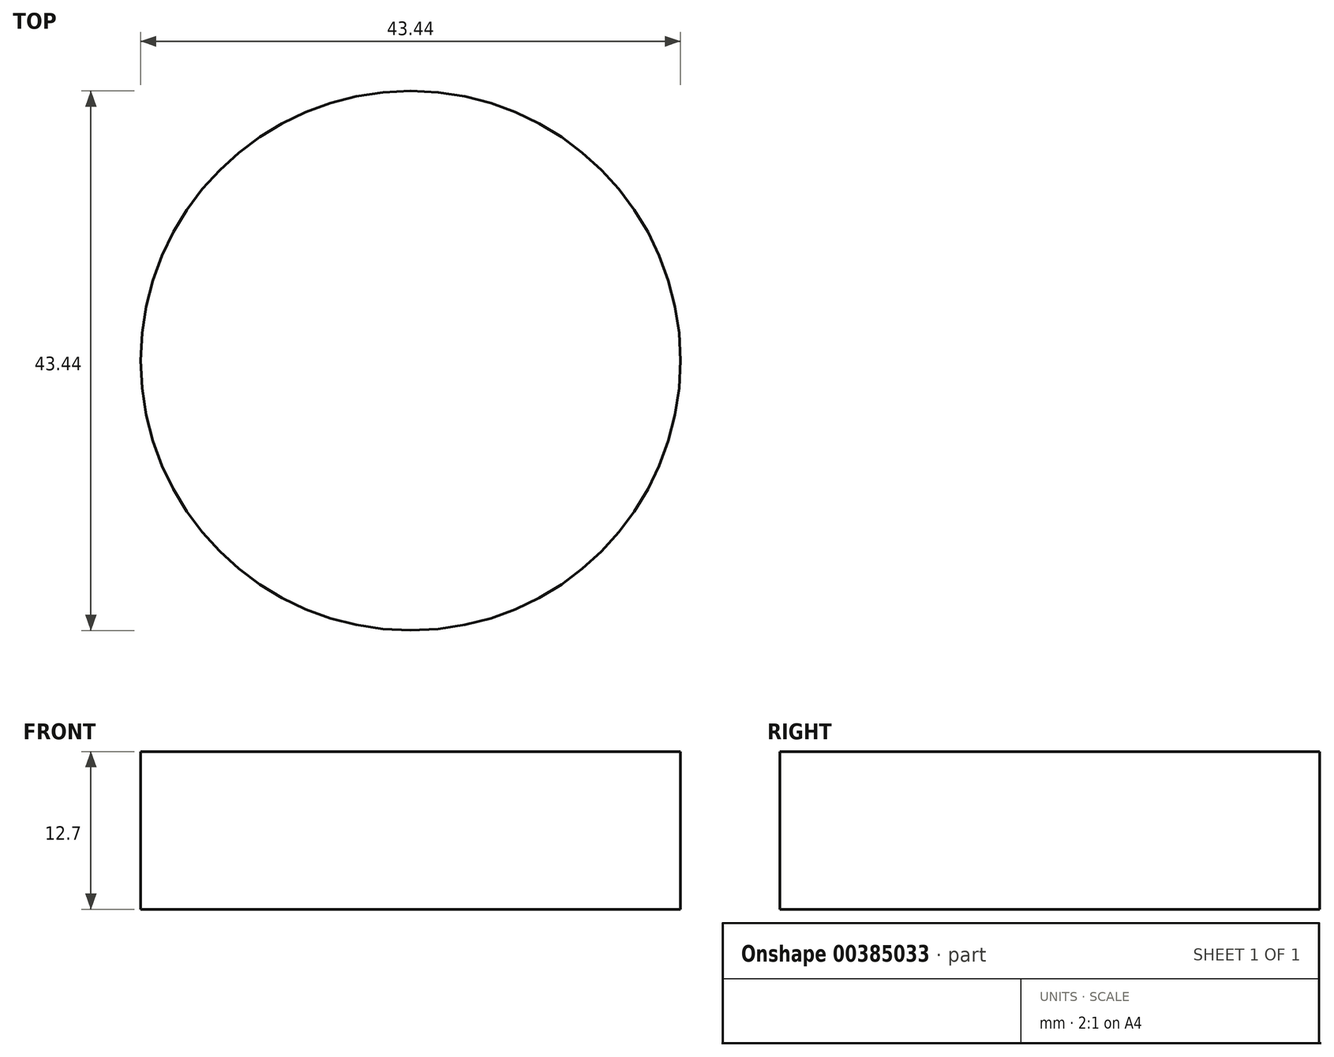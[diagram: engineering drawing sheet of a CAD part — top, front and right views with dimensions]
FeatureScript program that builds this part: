
annotation { "Feature Type Name" : "Feature", "Feature Type Description" : "" }
export const myFeature = defineFeature(function(context is Context, id is Id, definition is map)
    precondition{}
    {
        {
            var Q0;
            Q0=qCreatedBy(makeId("Top.planeOp"),FACE);
            var sketch = newSketch(context, id + "F0", { "sketchPlane" : qUnion([Q0])});
            skCircle(sketch, "E0", {"center": v(0, 0) * mm, "radius": 21.72 * mm});
            skSolve(sketch);
        }
        {
            var Q0;
            Q0=makeQuery(id+"F0.imprint","IMPRINT",FACE,{"disambiguationData":[TD([[makeQuery(id+"F0.imprint","IMPRINT",EDGE,{"derivedFrom":sQuery(id+"F0.wireOp",EDGE,"E0")}),1.0]])]});
            extrude(context, id + "F1", {"entities" : qUnion([Q0]), "depth" : 12.7 * mm});
        }
        {
            var Q0;
            Q0=qCreatedBy(makeId("Top.planeOp"),FACE);
            cPlane(context, id + "F2", {"entities" : qUnion([Q0]), "cplaneType" : CPlaneType.OFFSET, "offset" : 50.8 * mm, "width" : 152.4 * mm, "height" : 152.4 * mm});
        }
    });
